# Revit family: CENTUM Gleitunterlage ohne Abhebesicherung stehend
name_source: partatom
category: HLS-Bauteile
revit_build: Autodesk Revit 2017 (Build: 20190508_0315(x64)
units: mm (PartAtom-declared; Revit-internal decimal feet)

## family parameters
Arbeitsebenenbasiert = Ja
Beim Laden mit Abzugskörper schneiden = Nein
Bemaßung runder Anschluss = Durchmesser verwenden
Gemeinsam genutzt = Ja
Immer vertikal = Nein
Raumberechnungspunkt = Nein
Teiletyp = Normal

## types (2) — shared parameters
Abhebesicherung = ohne Abhebesicherung
Ausrichtung = stehend
Breite Gleitstreifen = 40 mm  [stored 0.131234 ft]
Breite Gleitunterlage = 110 mm
C = 17 mm
Fabrikat = MEFA
Firma = MEFA Befestigungs- und Montagesysteme GmbH
Gleitreibungsfaktor = 0,15
Gleitstreifen = MEFA Gleitstreifen : Gleitstreifen  76x 40x 2
Haftreibungsfaktor = 0,2
Kurztext2 = stehend ohne Abhebesicherung
Langloch = 14x40 mm
Länge Gleitstreifen = 76 mm  [stored 0.249344 ft]
Länge Gleitunterlage = 70 mm  [stored 0.229659 ft]
Sicherheitsfaktor = 1.54
Stärke = 16 mm
Vorgabe-Ansicht = 1219 mm
max. Stärke Gleitplatte = 16 mm
max. Temperaturbeständigkeit = 80 °C
max. zul. Last (Paar) = 40 kN

## per-type parameters (varying)
| type | Artikelnummer | EAN | Einfachanschluss | Gewicht | Gewicht pro Bauteil | Höhe | Höhe Gleitunterlage | Kurztext1 | Mengeneinheit | Profiltyp | vpe |
| CENTUM Gleitunterlage ohne Abhebesicherung XL100/XL200 stehend | 1651001010 | 4250928437211 | TL-XL Einfachanschluss stehend : Einfachanschluss XL100 stehend (9000594) | 1.07 kg | 1.07 kg | 74 mm | 74 mm | Gleitunterlage CENTUM XL 100 | St | XL 100, XL 200 | 1 St |
| CENTUM Gleitunterlage ohne Abhebesicherung XL120 stehend | 1651201030 | 4250928437242 | TL-XL Einfachanschluss stehend : Einfachanschluss XL120 stehend hoch (9000595) | 1.28 kg | 1.28 kg | 84 mm | 84 mm | Gleitunterlage CENTUM XL 120 | SET | XL 120 | 1 SET |

note: [stored X ft] marks values corroborated as IEEE doubles in the binary element streams (Revit-internal decimal feet)
